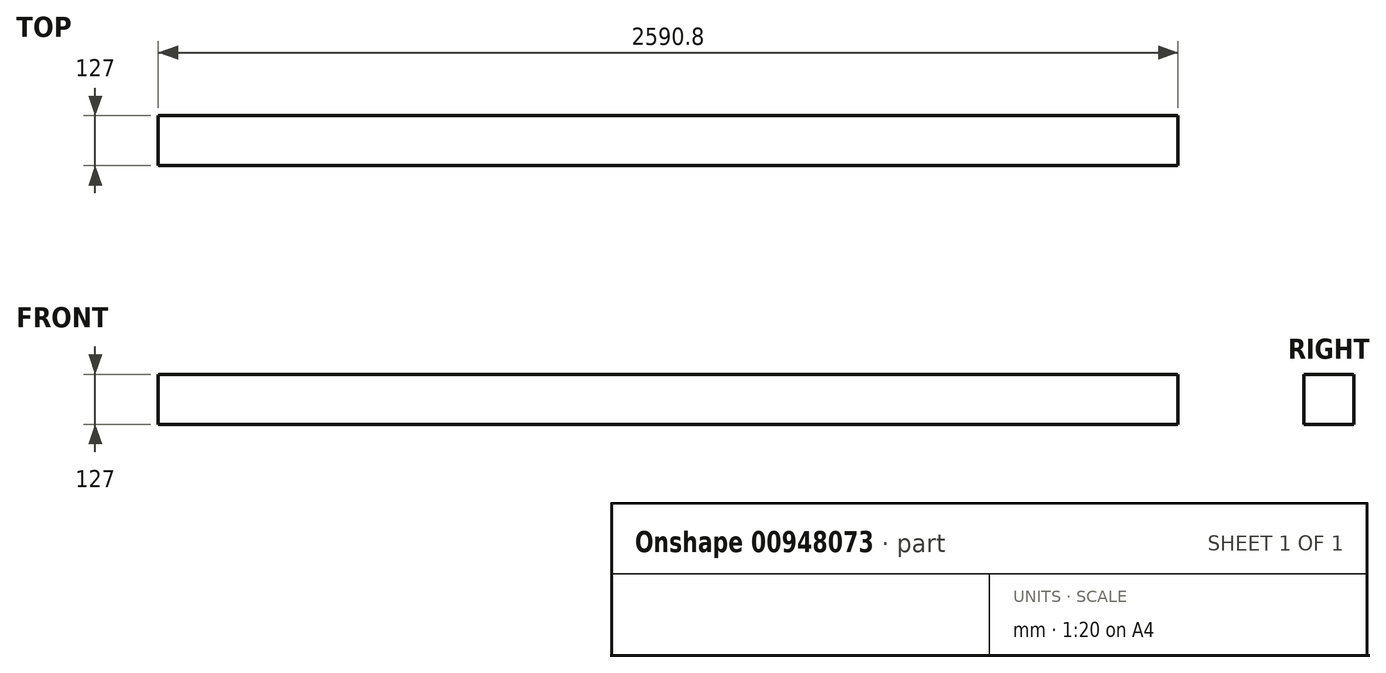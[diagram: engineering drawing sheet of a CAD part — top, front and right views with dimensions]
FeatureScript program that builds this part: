
annotation { "Feature Type Name" : "Feature", "Feature Type Description" : "" }
export const myFeature = defineFeature(function(context is Context, id is Id, definition is map)
    precondition{}
    {
        {
            var Q0;
            Q0=qCreatedBy(makeId("Right.planeOp"),FACE);
            var sketch = newSketch(context, id + "F0", { "sketchPlane" : qUnion([Q0])});
            skLineSegment(sketch, "E0.bottom", {"start": v(63.5, 63.5) * mm, "end": v(-63.5, 63.5) * mm});
            skLineSegment(sketch, "E0.top", {"start": v(63.5, -63.5) * mm, "end": v(-63.5, -63.5) * mm});
            skLineSegment(sketch, "E0.left", {"start": v(63.5, 63.5) * mm, "end": v(63.5, -63.5) * mm});
            skLineSegment(sketch, "E0.right", {"start": v(-63.5, 63.5) * mm, "end": v(-63.5, -63.5) * mm});
            skPoint(sketch, "E0.middle", {"position": v(0, 0) * mm});
            skSolve(sketch);
        }
        {
            var Q0;
            Q0=makeQuery(id+"F0.imprint","IMPRINT",FACE,{"disambiguationData":[TD([[makeQuery(id+"F0.imprint","IMPRINT",EDGE,{"derivedFrom":sQuery(id+"F0.wireOp",EDGE,"E0.bottom")}),1.0]])]});
            extrude(context, id + "F1", {"entities" : qUnion([Q0]), "endBound" : BoundingType.SYMMETRIC, "depth" : 2590.8 * mm, "offsetDistance" : 25.4 * mm, "hasSecondDirection" : true, "secondDirectionOppositeDirection" : true, "secondDirectionDepth" : 25.4 * mm});
        }
    });
